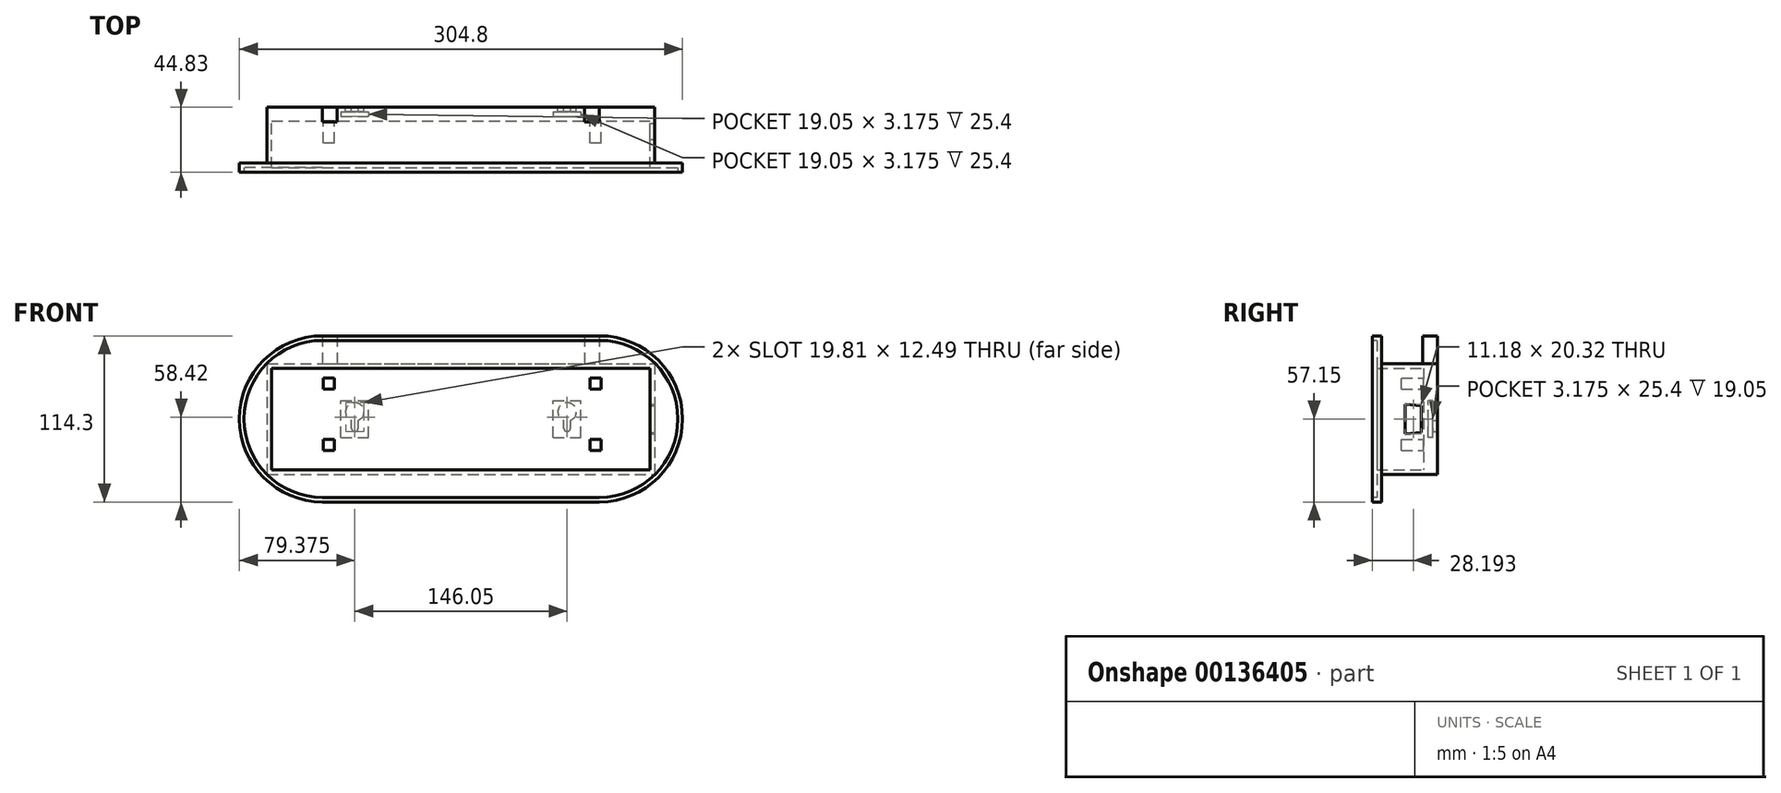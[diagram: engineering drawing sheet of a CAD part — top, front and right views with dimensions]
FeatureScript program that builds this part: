
annotation { "Feature Type Name" : "Feature", "Feature Type Description" : "" }
export const myFeature = defineFeature(function(context is Context, id is Id, definition is map)
    precondition{}
    {
        {
            var Q0;
            Q0=qCreatedBy(makeId("Front.planeOp"),FACE);
            var sketch = newSketch(context, id + "F0", { "sketchPlane" : qUnion([Q0])});
            skLineSegment(sketch, "E0.bottom", {"start": v(0, 0) * mm, "end": v(266.7, 0) * mm});
            skLineSegment(sketch, "E0.top", {"start": v(0, -76.2) * mm, "end": v(266.7, -76.2) * mm});
            skLineSegment(sketch, "E0.left", {"start": v(0, 0) * mm, "end": v(0, -76.2) * mm});
            skLineSegment(sketch, "E0.right", {"start": v(266.7, 0) * mm, "end": v(266.7, -76.2) * mm});
            skSolve(sketch);
        }
        {
            var Q0;
            Q0 = qSketchRegion(id + "F0", true);
            extrude(context, id + "F1", {"entities" : qUnion([Q0]), "depth" : 3.17 * mm});
        }
        {
            var Q0;
            Q0=makeQuery(id+"F1.opExtrude","CAP_FACE",FACE,{"disambiguationData":[OSD([sQuery(id+"F0.wireOp",EDGE,"E0.bottom"),sQuery(id+"F0.wireOp",EDGE,"E0.top"),sQuery(id+"F0.wireOp",EDGE,"E0.left"),sQuery(id+"F0.wireOp",EDGE,"E0.right")])],"isStart":false});
            var sketch = newSketch(context, id + "F2", { "sketchPlane" : qUnion([Q0])});
            skLineSegment(sketch, "E1.bottom", {"start": v(0, 0) * mm, "end": v(266.7, 0) * mm});
            skLineSegment(sketch, "E1.top", {"start": v(0, -76.2) * mm, "end": v(266.7, -76.2) * mm});
            skLineSegment(sketch, "E1.left", {"start": v(0, 0) * mm, "end": v(0, -76.2) * mm});
            skLineSegment(sketch, "E1.right", {"start": v(266.7, 0) * mm, "end": v(266.7, -76.2) * mm});
            skLineSegment(sketch, "E2.bottom", {"start": v(3.18, -3.18) * mm, "end": v(263.53, -3.18) * mm});
            skLineSegment(sketch, "E2.top", {"start": v(3.18, -73.03) * mm, "end": v(263.53, -73.03) * mm});
            skLineSegment(sketch, "E2.left", {"start": v(3.18, -3.17) * mm, "end": v(3.18, -73.03) * mm});
            skLineSegment(sketch, "E2.right", {"start": v(263.53, -3.18) * mm, "end": v(263.53, -73.03) * mm});
            skSolve(sketch);
        }
        {
            var Q0;
            Q0 = qSketchRegion(id + "F2", true);
            extrude(context, id + "F3", {"entities" : qUnion([Q0]), "operationType" : NewBodyOperationType.ADD, "depth" : 28.96 * mm});
        }
        {
            var Q0;
            Q0=makeQuery(id+"F3.opExtrude","CAP_FACE",FACE,{"disambiguationData":[OSD([sQuery(id+"F2.wireOp",EDGE,"E1.bottom"),sQuery(id+"F2.wireOp",EDGE,"E1.top"),sQuery(id+"F2.wireOp",EDGE,"E1.left"),sQuery(id+"F2.wireOp",EDGE,"E1.right"),sQuery(id+"F2.wireOp",EDGE,"E2.bottom"),sQuery(id+"F2.wireOp",EDGE,"E2.top"),sQuery(id+"F2.wireOp",EDGE,"E2.left"),sQuery(id+"F2.wireOp",EDGE,"E2.right")])],"isStart":false});
            var sketch = newSketch(context, id + "F4", { "sketchPlane" : qUnion([Q0])});
            skLineSegment(sketch, "E3", {"start": v(38.1, 19.05) * mm, "end": v(228.6, 19.05) * mm});
            skLineSegment(sketch, "E4", {"start": v(38.1, -95.25) * mm, "end": v(228.6, -95.25) * mm});
            skArc(sketch, "E5", {"start": v(38.1, 19.05) * mm, "mid": v(-19.05, -38.1) * mm, "end": v(38.1, -95.25) * mm});
            skArc(sketch, "E6", {"start": v(228.6, 19.05) * mm, "mid": v(285.75, -38.1) * mm, "end": v(228.6, -95.25) * mm});
            skLineSegment(sketch, "E7", {"start": v(285.75, -38.1) * mm, "end": v(266.7, -38.1) * mm, "construction": true});
            skLineSegment(sketch, "E8", {"start": v(-19.05, -38.1) * mm, "end": v(0, -38.1) * mm, "construction": true});
            skLineSegment(sketch, "E9.bottom", {"start": v(3.18, -73.03) * mm, "end": v(263.53, -73.03) * mm});
            skLineSegment(sketch, "E9.top", {"start": v(3.18, -3.18) * mm, "end": v(263.53, -3.18) * mm});
            skLineSegment(sketch, "E9.left", {"start": v(3.18, -73.03) * mm, "end": v(3.18, -3.17) * mm});
            skLineSegment(sketch, "E9.right", {"start": v(263.53, -73.03) * mm, "end": v(263.53, -3.17) * mm});
            skSolve(sketch);
        }
        {
            var Q0;
            Q0 = qSketchRegion(id + "F4", true);
            extrude(context, id + "F5", {"entities" : qUnion([Q0]), "operationType" : NewBodyOperationType.ADD, "depth" : 6.35 * mm});
        }
        {
            var Q0;
            Q0=makeQuery(id+"F5.opExtrude","CAP_FACE",FACE,{"disambiguationData":[OSD([sQuery(id+"F4.wireOp",EDGE,"E3"),sQuery(id+"F4.wireOp",EDGE,"E4"),sQuery(id+"F4.wireOp",EDGE,"E5"),sQuery(id+"F4.wireOp",EDGE,"E6"),sQuery(id+"F4.wireOp",EDGE,"E9.bottom"),sQuery(id+"F4.wireOp",EDGE,"E9.top"),sQuery(id+"F4.wireOp",EDGE,"E9.left"),sQuery(id+"F4.wireOp",EDGE,"E9.right")])],"isStart":false});
            var sketch = newSketch(context, id + "F6", { "sketchPlane" : qUnion([Q0])});
            skLineSegment(sketch, "E10", {"start": v(38.1, 15.87) * mm, "end": v(228.6, 15.88) * mm});
            skLineSegment(sketch, "E11", {"start": v(38.1, -92.08) * mm, "end": v(228.6, -92.08) * mm});
            skArc(sketch, "E12", {"start": v(38.1, 15.87) * mm, "mid": v(-15.88, -38.1) * mm, "end": v(38.1, -92.08) * mm});
            skArc(sketch, "E13", {"start": v(228.6, 15.88) * mm, "mid": v(282.58, -38.1) * mm, "end": v(228.6, -92.08) * mm});
            skSolve(sketch);
        }
        {
            var Q0;
            Q0 = qSketchRegion(id + "F6", true);
            extrude(context, id + "F7", {"entities" : qUnion([Q0]), "operationType" : NewBodyOperationType.REMOVE, "oppositeDirection" : true, "depth" : 3.17 * mm});
        }
        {
            var Q0;
            Q0=makeQuery(id+"F1.opExtrude","CAP_FACE",FACE,{"disambiguationData":[OSD([sQuery(id+"F0.wireOp",EDGE,"E0.bottom"),sQuery(id+"F0.wireOp",EDGE,"E0.top"),sQuery(id+"F0.wireOp",EDGE,"E0.left"),sQuery(id+"F0.wireOp",EDGE,"E0.right")])],"isStart":true});
            var sketch = newSketch(context, id + "F8", { "sketchPlane" : qUnion([Q0])});
            skLineSegment(sketch, "E14.bottom", {"start": v(-50.8, -50.8) * mm, "end": v(-69.85, -50.8) * mm});
            skLineSegment(sketch, "E14.top", {"start": v(-50.8, -25.4) * mm, "end": v(-69.85, -25.4) * mm});
            skLineSegment(sketch, "E14.left", {"start": v(-50.8, -50.8) * mm, "end": v(-50.8, -25.4) * mm});
            skLineSegment(sketch, "E14.right", {"start": v(-69.85, -50.8) * mm, "end": v(-69.85, -25.4) * mm});
            skLineSegment(sketch, "E15.bottom", {"start": v(-196.85, -50.8) * mm, "end": v(-215.9, -50.8) * mm});
            skLineSegment(sketch, "E15.top", {"start": v(-196.85, -25.4) * mm, "end": v(-215.9, -25.4) * mm});
            skLineSegment(sketch, "E15.left", {"start": v(-196.85, -50.8) * mm, "end": v(-196.85, -25.4) * mm});
            skLineSegment(sketch, "E15.right", {"start": v(-215.9, -50.8) * mm, "end": v(-215.9, -25.4) * mm});
            skLineSegment(sketch, "E16", {"start": v(-60.33, -50.8) * mm, "end": v(-60.33, -76.2) * mm, "construction": true});
            skLineSegment(sketch, "E17", {"start": v(-60.33, -25.4) * mm, "end": v(-60.33, 0) * mm, "construction": true});
            skLineSegment(sketch, "E18", {"start": v(-50.8, -38.1) * mm, "end": v(0, -38.1) * mm, "construction": true});
            skLineSegment(sketch, "E19", {"start": v(-215.9, -38.1) * mm, "end": v(-266.7, -38.1) * mm, "construction": true});
            skLineSegment(sketch, "E20.bottom", {"start": v(0, -76.2) * mm, "end": v(-266.7, -76.2) * mm});
            skLineSegment(sketch, "E20.top", {"start": v(0, 0) * mm, "end": v(-266.7, 0) * mm});
            skLineSegment(sketch, "E20.left", {"start": v(0, -76.2) * mm, "end": v(0, 0) * mm});
            skLineSegment(sketch, "E20.right", {"start": v(-266.7, -76.2) * mm, "end": v(-266.7, 0) * mm});
            skSolve(sketch);
        }
        {
            var Q0;
            Q0 = qSketchRegion(id + "F8", true);
            extrude(context, id + "F9", {"entities" : qUnion([Q0]), "operationType" : NewBodyOperationType.ADD, "depth" : 6.35 * mm});
        }
        {
            var Q0;
            Q0=makeQuery(id+"F9.opExtrude","CAP_FACE",FACE,{"disambiguationData":[OSD([sQuery(id+"F8.wireOp",EDGE,"E14.bottom"),sQuery(id+"F8.wireOp",EDGE,"E14.top"),sQuery(id+"F8.wireOp",EDGE,"E14.left"),sQuery(id+"F8.wireOp",EDGE,"E14.right"),sQuery(id+"F8.wireOp",EDGE,"E15.bottom"),sQuery(id+"F8.wireOp",EDGE,"E15.top"),sQuery(id+"F8.wireOp",EDGE,"E15.left"),sQuery(id+"F8.wireOp",EDGE,"E15.right"),sQuery(id+"F8.wireOp",EDGE,"E20.bottom"),sQuery(id+"F8.wireOp",EDGE,"E20.top"),sQuery(id+"F8.wireOp",EDGE,"E20.left"),sQuery(id+"F8.wireOp",EDGE,"E20.right")])],"isStart":false});
            var sketch = newSketch(context, id + "F10", { "sketchPlane" : qUnion([Q0])});
            skLineSegment(sketch, "E21.bottom", {"start": v(-50.8, -50.8) * mm, "end": v(-69.85, -50.8) * mm});
            skLineSegment(sketch, "E21.top", {"start": v(-50.8, -25.4) * mm, "end": v(-69.85, -25.4) * mm});
            skLineSegment(sketch, "E21.left", {"start": v(-50.8, -50.8) * mm, "end": v(-50.8, -25.4) * mm});
            skLineSegment(sketch, "E21.right", {"start": v(-69.85, -50.8) * mm, "end": v(-69.85, -25.4) * mm});
            skLineSegment(sketch, "E22.bottom", {"start": v(-196.85, -50.8) * mm, "end": v(-215.9, -50.8) * mm});
            skLineSegment(sketch, "E22.top", {"start": v(-196.85, -25.4) * mm, "end": v(-215.9, -25.4) * mm});
            skLineSegment(sketch, "E22.left", {"start": v(-196.85, -50.8) * mm, "end": v(-196.85, -25.4) * mm});
            skLineSegment(sketch, "E22.right", {"start": v(-215.9, -50.8) * mm, "end": v(-215.9, -25.4) * mm});
            skArc(sketch, "E23", {"start": v(-58.04, -39.2) * mm, "mid": v(-60.33, -26.92) * mm, "end": v(-62.61, -39.2) * mm});
            skPoint(sketch, "E23.centerSnap0", {"position": v(-60.33, -50.8) * mm});
            skArc(sketch, "E24", {"start": v(-204.09, -39.2) * mm, "mid": v(-206.37, -26.92) * mm, "end": v(-208.66, -39.2) * mm});
            skPoint(sketch, "E24.centerSnap0", {"position": v(-206.37, -50.8) * mm});
            skArc(sketch, "E25", {"start": v(-62.61, -44.45) * mm, "mid": v(-60.33, -46.74) * mm, "end": v(-58.04, -44.45) * mm});
            skArc(sketch, "E26", {"start": v(-208.66, -44.45) * mm, "mid": v(-206.37, -46.74) * mm, "end": v(-204.09, -44.45) * mm});
            skLineSegment(sketch, "E27", {"start": v(-208.66, -44.45) * mm, "end": v(-208.66, -39.2) * mm});
            skLineSegment(sketch, "E28", {"start": v(-204.09, -44.45) * mm, "end": v(-204.09, -39.2) * mm});
            skLineSegment(sketch, "E29", {"start": v(-62.61, -44.45) * mm, "end": v(-62.61, -39.2) * mm});
            skLineSegment(sketch, "E30", {"start": v(-58.04, -44.45) * mm, "end": v(-58.04, -39.2) * mm});
            skSolve(sketch);
        }
        {
            var Q0;
            Q0 = qSketchRegion(id + "F10", true);
            extrude(context, id + "F11", {"entities" : qUnion([Q0]), "operationType" : NewBodyOperationType.ADD, "oppositeDirection" : true, "depth" : 3.17 * mm});
        }
        {
            var Q0;
            Q0=makeQuery(id+"F9.boolean.opBoolean","MERGE",FACE,{"derivedFrom":[makeQuery(id+"F3.boolean.opBoolean","MERGE",FACE,{"derivedFrom":[makeQuery(id+"F1.opExtrude","SWEPT_FACE",FACE,{"disambiguationData":[OSD([sQuery(id+"F0.wireOp",EDGE,"E0.right")])]}),makeQuery(id+"F3.opExtrude","SWEPT_FACE",FACE,{"disambiguationData":[OSD([sQuery(id+"F2.wireOp",EDGE,"E1.right")])]})]}),makeQuery(id+"F9.opExtrude","SWEPT_FACE",FACE,{"disambiguationData":[OSD([sQuery(id+"F8.wireOp",EDGE,"E20.right")])]})]});
            var sketch = newSketch(context, id + "F12", { "sketchPlane" : qUnion([Q0])});
            skLineSegment(sketch, "E31", {"start": v(-4.7, -28.9) * mm, "end": v(-4.7, -47.3) * mm});
            skLineSegment(sketch, "E32", {"start": v(-15.88, -27.94) * mm, "end": v(-15.88, -48.26) * mm});
            skLineSegment(sketch, "E33", {"start": v(-4.7, -28.9) * mm, "end": v(-15.88, -27.94) * mm});
            skLineSegment(sketch, "E34", {"start": v(-4.7, -47.3) * mm, "end": v(-15.88, -48.26) * mm});
            skLineSegment(sketch, "E35", {"start": v(-4.7, -38.1) * mm, "end": v(-15.88, -38.1) * mm, "construction": true});
            skLineSegment(sketch, "E36", {"start": v(-10.29, -38.1) * mm, "end": v(-10.29, -76.2) * mm, "construction": true});
            skLineSegment(sketch, "E37", {"start": v(-10.29, -38.1) * mm, "end": v(-10.29, 0) * mm, "construction": true});
            skSolve(sketch);
        }
        {
            var Q0;
            Q0 = qSketchRegion(id + "F12", true);
            extrude(context, id + "F13", {"entities" : qUnion([Q0]), "operationType" : NewBodyOperationType.REMOVE, "endBound" : BoundingType.UP_TO_NEXT, "oppositeDirection" : true, "depth" : 25.4 * mm});
        }
        {
            var Q0;
            Q0=makeQuery(id+"F9.boolean.opBoolean","MERGE",FACE,{"derivedFrom":[makeQuery(id+"F3.boolean.opBoolean","MERGE",FACE,{"derivedFrom":[makeQuery(id+"F1.opExtrude","SWEPT_FACE",FACE,{"disambiguationData":[OSD([sQuery(id+"F0.wireOp",EDGE,"E0.bottom")])]}),makeQuery(id+"F3.opExtrude","SWEPT_FACE",FACE,{"disambiguationData":[OSD([sQuery(id+"F2.wireOp",EDGE,"E1.bottom")])]})]}),makeQuery(id+"F9.opExtrude","SWEPT_FACE",FACE,{"disambiguationData":[OSD([sQuery(id+"F8.wireOp",EDGE,"E20.top")])]})]});
            var sketch = newSketch(context, id + "F14", { "sketchPlane" : qUnion([Q0])});
            skLineSegment(sketch, "E38.bottom", {"start": v(38.1, 6.35) * mm, "end": v(48.26, 6.35) * mm});
            skLineSegment(sketch, "E38.top", {"start": v(38.1, -3.81) * mm, "end": v(48.26, -3.81) * mm});
            skLineSegment(sketch, "E38.left", {"start": v(38.1, 6.35) * mm, "end": v(38.1, -3.81) * mm});
            skLineSegment(sketch, "E38.right", {"start": v(48.26, 6.35) * mm, "end": v(48.26, -3.81) * mm});
            skLineSegment(sketch, "E39.bottom", {"start": v(218.44, -3.8) * mm, "end": v(228.6, -3.8) * mm});
            skLineSegment(sketch, "E39.top", {"start": v(218.44, 6.35) * mm, "end": v(228.6, 6.35) * mm});
            skLineSegment(sketch, "E39.left", {"start": v(218.44, -3.8) * mm, "end": v(218.44, 6.35) * mm});
            skLineSegment(sketch, "E39.right", {"start": v(228.6, -3.8) * mm, "end": v(228.6, 6.35) * mm});
            skSolve(sketch);
        }
        {
            var Q0;
            Q0 = qSketchRegion(id + "F14", true);
            var Q1;
            Q1=makeQuery(id+"F5.opExtrude","SWEPT_FACE",FACE,{"disambiguationData":[OSD([sQuery(id+"F4.wireOp",EDGE,"E3")])]});
            extrude(context, id + "F15", {"entities" : qUnion([Q0]), "operationType" : NewBodyOperationType.ADD, "endBound" : BoundingType.UP_TO_SURFACE, "endBoundEntityFace" : qUnion([Q1]), "depth" : 25.4 * mm});
        }
        {
            var Q0;
            Q0=makeQuery(id+"F1.opExtrude","CAP_FACE",FACE,{"disambiguationData":[OSD([sQuery(id+"F0.wireOp",EDGE,"E0.bottom"),sQuery(id+"F0.wireOp",EDGE,"E0.top"),sQuery(id+"F0.wireOp",EDGE,"E0.left"),sQuery(id+"F0.wireOp",EDGE,"E0.right")])],"isStart":false});
            var sketch = newSketch(context, id + "F16", { "sketchPlane" : qUnion([Q0])});
            skLineSegment(sketch, "E40.bottom", {"start": v(229.82, -59.82) * mm, "end": v(222.2, -59.82) * mm});
            skLineSegment(sketch, "E40.top", {"start": v(229.82, -52.2) * mm, "end": v(222.2, -52.2) * mm});
            skLineSegment(sketch, "E40.left", {"start": v(229.82, -59.82) * mm, "end": v(229.82, -52.2) * mm});
            skLineSegment(sketch, "E40.right", {"start": v(222.2, -59.82) * mm, "end": v(222.2, -52.2) * mm});
            skLineSegment(sketch, "E41.bottom", {"start": v(229.82, -17.65) * mm, "end": v(222.2, -17.65) * mm});
            skLineSegment(sketch, "E41.top", {"start": v(229.82, -10.03) * mm, "end": v(222.2, -10.03) * mm});
            skLineSegment(sketch, "E41.left", {"start": v(229.82, -17.65) * mm, "end": v(229.82, -10.03) * mm});
            skLineSegment(sketch, "E41.right", {"start": v(222.2, -17.65) * mm, "end": v(222.2, -10.03) * mm});
            skLineSegment(sketch, "E42.bottom", {"start": v(46.36, -59.82) * mm, "end": v(38.73, -59.82) * mm});
            skLineSegment(sketch, "E42.top", {"start": v(46.36, -52.2) * mm, "end": v(38.73, -52.2) * mm});
            skLineSegment(sketch, "E42.left", {"start": v(46.36, -59.82) * mm, "end": v(46.36, -52.2) * mm});
            skLineSegment(sketch, "E42.right", {"start": v(38.73, -59.82) * mm, "end": v(38.73, -52.2) * mm});
            skLineSegment(sketch, "E43.bottom", {"start": v(46.36, -17.65) * mm, "end": v(38.73, -17.65) * mm});
            skLineSegment(sketch, "E43.top", {"start": v(46.36, -10.03) * mm, "end": v(38.73, -10.03) * mm});
            skLineSegment(sketch, "E43.left", {"start": v(46.35, -17.65) * mm, "end": v(46.35, -10.03) * mm});
            skLineSegment(sketch, "E43.right", {"start": v(38.73, -17.65) * mm, "end": v(38.73, -10.03) * mm});
            skLineSegment(sketch, "E44", {"start": v(226, -55.74) * mm, "end": v(42.55, -55.74) * mm, "construction": true});
            skPoint(sketch, "E44.startSnap0", {"position": v(226, -59.82) * mm});
            skPoint(sketch, "E44.endSnap0", {"position": v(42.55, -59.82) * mm});
            skLineSegment(sketch, "E45", {"start": v(232, -13.84) * mm, "end": v(232, -56) * mm, "construction": true});
            skPoint(sketch, "E45.startSnap0", {"position": v(222.2, -13.84) * mm});
            skPoint(sketch, "E45.endSnap0", {"position": v(229.82, -56) * mm});
            skSolve(sketch);
        }
        {
            var Q0;
            Q0 = qSketchRegion(id + "F16", true);
            extrude(context, id + "F17", {"entities" : qUnion([Q0]), "operationType" : NewBodyOperationType.ADD, "depth" : 15.24 * mm});
        }
    });
